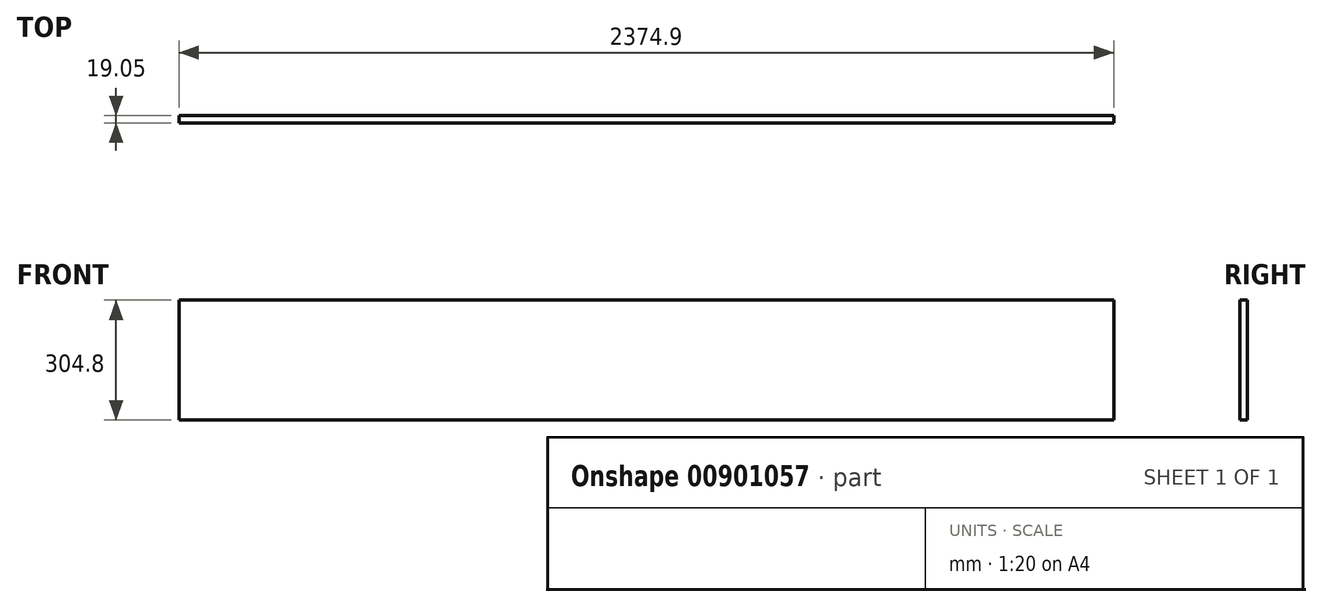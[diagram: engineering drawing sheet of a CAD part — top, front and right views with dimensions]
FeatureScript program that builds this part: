
annotation { "Feature Type Name" : "Feature", "Feature Type Description" : "" }
export const myFeature = defineFeature(function(context is Context, id is Id, definition is map)
    precondition{}
    {
        {
            var Q0;
            Q0=qCreatedBy(makeId("Front.planeOp"),FACE);
            var sketch = newSketch(context, id + "F0", { "sketchPlane" : qUnion([Q0])});
            skLineSegment(sketch, "E0.bottom", {"start": v(-1187.45, 152.4) * mm, "end": v(1187.45, 152.4) * mm});
            skLineSegment(sketch, "E0.top", {"start": v(-1187.45, -152.4) * mm, "end": v(1187.45, -152.4) * mm});
            skLineSegment(sketch, "E0.left", {"start": v(-1187.45, 152.4) * mm, "end": v(-1187.45, -152.4) * mm});
            skLineSegment(sketch, "E0.right", {"start": v(1187.45, 152.4) * mm, "end": v(1187.45, -152.4) * mm});
            skPoint(sketch, "E0.middle", {"position": v(0, 0) * mm});
            skSolve(sketch);
        }
        {
            var Q0;
            Q0=makeQuery(id+"F0.imprint","IMPRINT",FACE,{"disambiguationData":[TD([[makeQuery(id+"F0.imprint","IMPRINT",EDGE,{"derivedFrom":sQuery(id+"F0.wireOp",EDGE,"E0.bottom")}),-1.0]])]});
            extrude(context, id + "F1", {"entities" : qUnion([Q0]), "depth" : 19.05 * mm, "offsetDistance" : 25.4 * mm});
        }
    });
